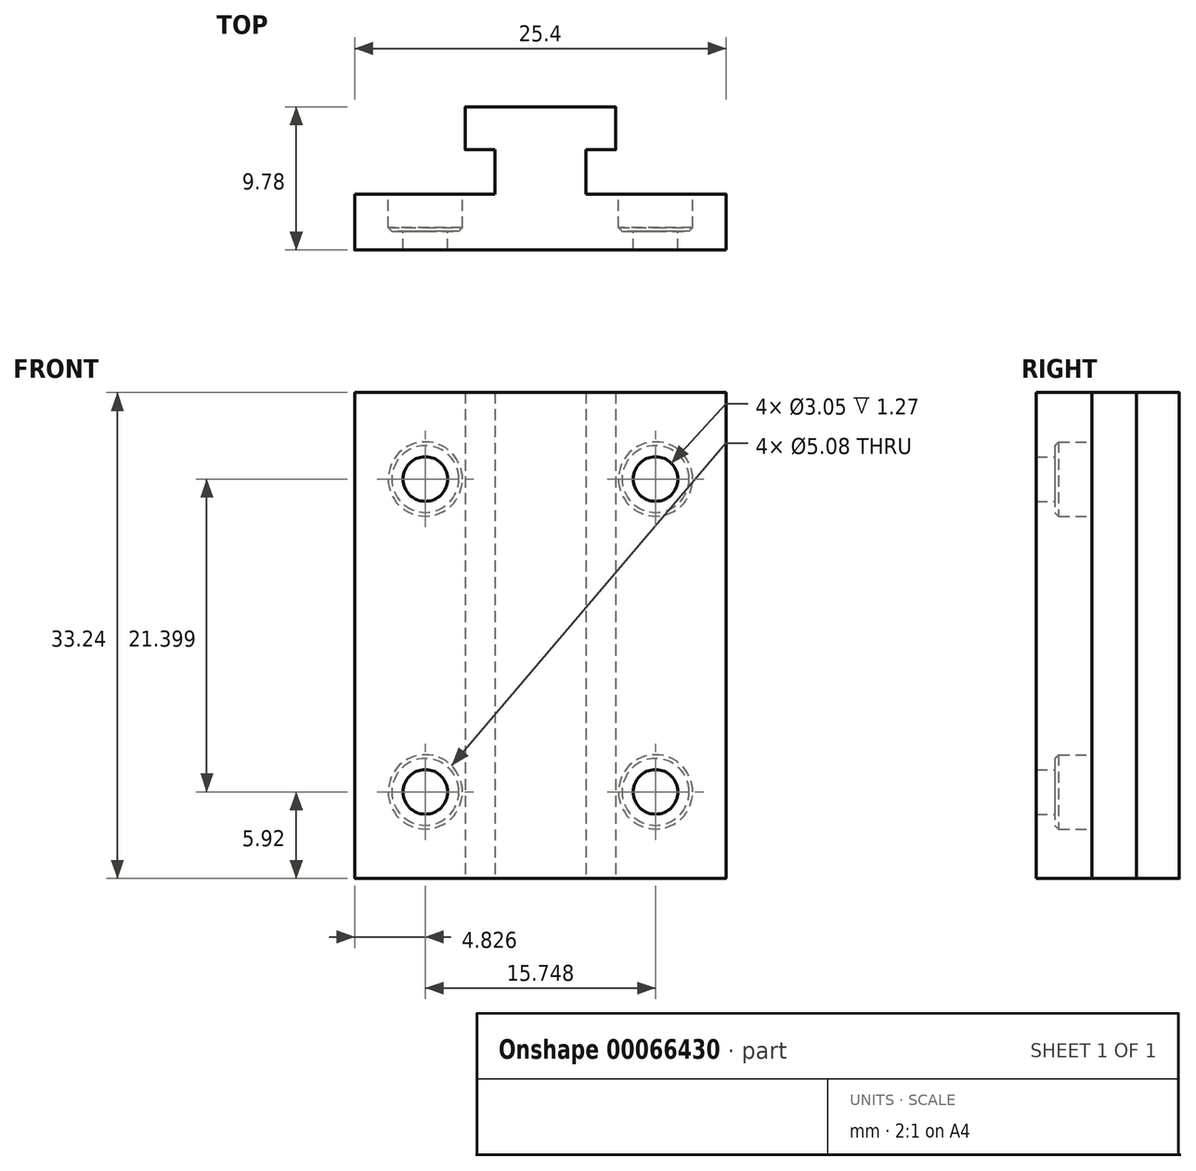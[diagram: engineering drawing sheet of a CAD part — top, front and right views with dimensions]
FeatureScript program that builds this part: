
annotation { "Feature Type Name" : "Feature", "Feature Type Description" : "" }
export const myFeature = defineFeature(function(context is Context, id is Id, definition is map)
    precondition{}
    {
        {
            var Q0;
            Q0=qCreatedBy(makeId("Front.planeOp"),FACE);
            var sketch = newSketch(context, id + "F0", { "sketchPlane" : qUnion([Q0])});
            skLineSegment(sketch, "E0.rect.bottom", {"start": v(5.16, 16.62) * mm, "end": v(-5.16, 16.62) * mm});
            skLineSegment(sketch, "E0.rect.top", {"start": v(5.16, -16.62) * mm, "end": v(-5.16, -16.62) * mm});
            skLineSegment(sketch, "E0.rect.left", {"start": v(5.16, 16.62) * mm, "end": v(5.16, -16.62) * mm});
            skLineSegment(sketch, "E0.rect.right", {"start": v(-5.16, 16.62) * mm, "end": v(-5.16, -16.62) * mm});
            skPoint(sketch, "E0.rect.middle", {"position": v(0, 0) * mm});
            skSolve(sketch);
        }
        {
            var Q0;
            Q0=qSketchRegion(id+"F0",true);
            extrude(context, id + "F1", {"entities" : qUnion([Q0]), "depth" : 2.92 * mm, "offsetDistance" : 25.4 * mm});
        }
        {
            var Q0;
            Q0=makeQuery(id+"F1.opExtrude","CAP_FACE",FACE,{"disambiguationData":[OSD([sQuery(id+"F0.wireOp",EDGE,"E0.rect.bottom"),sQuery(id+"F0.wireOp",EDGE,"E0.rect.top"),sQuery(id+"F0.wireOp",EDGE,"E0.rect.left"),sQuery(id+"F0.wireOp",EDGE,"E0.rect.right")])],"isStart":false});
            var sketch = newSketch(context, id + "F2", { "sketchPlane" : qUnion([Q0])});
            skLineSegment(sketch, "E1.rect.bottom", {"start": v(3.1, 16.62) * mm, "end": v(-3.1, 16.62) * mm});
            skLineSegment(sketch, "E1.rect.top", {"start": v(3.1, -16.62) * mm, "end": v(-3.1, -16.62) * mm});
            skLineSegment(sketch, "E1.rect.left", {"start": v(3.1, 16.62) * mm, "end": v(3.1, -16.62) * mm});
            skLineSegment(sketch, "E1.rect.right", {"start": v(-3.1, 16.62) * mm, "end": v(-3.1, -16.62) * mm});
            skPoint(sketch, "E1.rect.middle", {"position": v(0, 0) * mm});
            skSolve(sketch);
        }
        {
            var Q0;
            Q0=qSketchRegion(id+"F2",true);
            extrude(context, id + "F3", {"entities" : qUnion([Q0]), "operationType" : NewBodyOperationType.ADD, "depth" : 3.05 * mm, "offsetDistance" : 25.4 * mm});
        }
        {
            var Q0;
            Q0=makeQuery(id+"F3.opExtrude","CAP_FACE",FACE,{"disambiguationData":[OSD([sQuery(id+"F2.wireOp",EDGE,"E1.rect.bottom"),sQuery(id+"F2.wireOp",EDGE,"E1.rect.top"),sQuery(id+"F2.wireOp",EDGE,"E1.rect.left"),sQuery(id+"F2.wireOp",EDGE,"E1.rect.right")])],"isStart":false});
            var sketch = newSketch(context, id + "F4", { "sketchPlane" : qUnion([Q0])});
            skLineSegment(sketch, "E2.bottom", {"start": v(-12.7, -16.62) * mm, "end": v(12.7, -16.62) * mm});
            skLineSegment(sketch, "E2.top", {"start": v(-12.7, 16.62) * mm, "end": v(12.7, 16.62) * mm});
            skLineSegment(sketch, "E2.left", {"start": v(-12.7, -16.62) * mm, "end": v(-12.7, 16.62) * mm});
            skLineSegment(sketch, "E2.right", {"start": v(12.7, -16.62) * mm, "end": v(12.7, 16.62) * mm});
            skCircle(sketch, "E3", {"center": v(7.87, 10.7) * mm, "radius": 1.52 * mm});
            skCircle(sketch, "E4", {"center": v(7.87, -10.7) * mm, "radius": 1.52 * mm});
            skCircle(sketch, "E5", {"center": v(-7.87, -10.7) * mm, "radius": 1.52 * mm});
            skCircle(sketch, "E6", {"center": v(-7.87, 10.7) * mm, "radius": 1.52 * mm});
            skLineSegment(sketch, "E7", {"start": v(-7.87, -10.7) * mm, "end": v(7.87, -10.7) * mm, "construction": true});
            skPoint(sketch, "E8", {"position": v(0, -10.7) * mm});
            skLineSegment(sketch, "E9", {"start": v(7.87, 10.7) * mm, "end": v(7.87, -10.7) * mm, "construction": true});
            skPoint(sketch, "E10", {"position": v(7.87, 0) * mm});
            skSolve(sketch);
        }
        {
            var Q0;
            Q0=qSketchRegion(id+"F4",true);
            extrude(context, id + "F5", {"entities" : qUnion([Q0]), "operationType" : NewBodyOperationType.ADD, "depth" : 3.8 * mm, "offsetDistance" : 25.4 * mm});
        }
        {
            var Q0;
            Q0=makeQuery(id+"F1.opExtrude","CAP_EDGE",EDGE,{"disambiguationData":[OSD([sQuery(id+"F0.wireOp",EDGE,"E0.rect.left")])],"isStart":false});
            var Q1;
            Q1=makeQuery(id+"F1.opExtrude","CAP_EDGE",EDGE,{"disambiguationData":[OSD([sQuery(id+"F0.wireOp",EDGE,"E0.rect.left")])],"isStart":true});
            var Q2;
            Q2=makeQuery(id+"F1.opExtrude","CAP_EDGE",EDGE,{"disambiguationData":[OSD([sQuery(id+"F0.wireOp",EDGE,"E0.rect.right")])],"isStart":false});
            var Q3;
            Q3=makeQuery(id+"F1.opExtrude","CAP_EDGE",EDGE,{"disambiguationData":[OSD([sQuery(id+"F0.wireOp",EDGE,"E0.rect.right")])],"isStart":true});
            var Q4;
            Q4=makeQuery(id+"F1.opExtrude","CAP_EDGE",EDGE,{"disambiguationData":[OSD([sQuery(id+"F0.wireOp",EDGE,"E0.rect.top")])],"isStart":true});
            var Q5;
            Q5=makeQuery(id+"F1.opExtrude","CAP_EDGE",EDGE,{"disambiguationData":[OSD([sQuery(id+"F0.wireOp",EDGE,"E0.rect.bottom")])],"isStart":true});
            var Q6;
            Q6=makeQuery(id+"F5.opExtrude","SWEPT_EDGE",EDGE,{"disambiguationData":[OSD([sQuery(id+"F4.wireOp",EDGE,"E2.bottom"),sQuery(id+"F4.wireOp",EDGE,"E2.right")])]});
            var Q7;
            Q7=makeQuery(id+"F5.opExtrude","SWEPT_EDGE",EDGE,{"disambiguationData":[OSD([sQuery(id+"F4.wireOp",EDGE,"E2.bottom"),sQuery(id+"F4.wireOp",EDGE,"E2.left")])]});
            var Q8;
            Q8=makeQuery(id+"F5.opExtrude","SWEPT_EDGE",EDGE,{"disambiguationData":[OSD([sQuery(id+"F4.wireOp",EDGE,"E2.top"),sQuery(id+"F4.wireOp",EDGE,"E2.left")])]});
            var Q9;
            Q9=makeQuery(id+"F5.opExtrude","SWEPT_EDGE",EDGE,{"disambiguationData":[OSD([sQuery(id+"F4.wireOp",EDGE,"E2.top"),sQuery(id+"F4.wireOp",EDGE,"E2.right")])]});
            fillet(context, id + "F6", {"entities" : qUnion([Q0, Q1, Q2, Q3, Q4, Q5, Q6, Q7, Q8, Q9]), "radius" : .63 / 50.8 * mm, "tangentPropagation" : true, "allowEdgeOverflow" : false});
        }
        {
            var Q0;
            {var subQ0=sQuery(id+"F4.wireOp",EDGE,"E3");var subQ1=sQuery(id+"F4.wireOp",EDGE,"E2.right");var subQ2=sQuery(id+"F4.wireOp",EDGE,"E2.bottom");var subQ3=sQuery(id+"F4.wireOp",EDGE,"E2.top");var subQ4=sQuery(id+"F4.wireOp",EDGE,"E4");Q0=makeQuery(id+"F5.boolean.opBoolean","SPLIT",FACE,{"disambiguationData":[TD([makeQuery(id+"F3.opExtrude","SWEPT_FACE",FACE,{"disambiguationData":[OSD([sQuery(id+"F2.wireOp",EDGE,"E1.rect.left")])]})])],"derivedFrom":makeQuery(id+"F5.opExtrude","CAP_FACE",FACE,{"disambiguationData":[OSD([subQ2,subQ3,sQuery(id+"F4.wireOp",EDGE,"E2.left"),subQ1,subQ0,subQ4,sQuery(id+"F4.wireOp",EDGE,"E5"),sQuery(id+"F4.wireOp",EDGE,"E6")])],"isStart":true})});}
            var sketch = newSketch(context, id + "F7", { "sketchPlane" : qUnion([Q0])});
            skCircle(sketch, "E11", {"center": v(-7.87, 10.7) * mm, "radius": 2.54 * mm});
            skCircle(sketch, "E12", {"center": v(7.87, -10.7) * mm, "radius": 2.54 * mm});
            skCircle(sketch, "E13", {"center": v(-7.87, -10.7) * mm, "radius": 2.54 * mm});
            skCircle(sketch, "E14", {"center": v(7.87, 10.7) * mm, "radius": 2.54 * mm});
            skSolve(sketch);
        }
        {
            var Q0;
            Q0 = qSketchRegion(id + "F7", true);
            extrude(context, id + "F8", {"entities" : qUnion([Q0]), "operationType" : NewBodyOperationType.REMOVE, "oppositeDirection" : true, "depth" : 2.54 * mm, "offsetDistance" : 25.4 * mm});
        }
        {
            var Q0;
            Q0=makeQuery(id+"F8.boolean.opBoolean","COPY",EDGE,{"derivedFrom":makeQuery(id+"F8.opExtrude","CAP_EDGE",EDGE,{"disambiguationData":[OSD([sQuery(id+"F7.wireOp",EDGE,"E14")])],"isStart":false})});
            var Q1;
            Q1=makeQuery(id+"F8.boolean.opBoolean","COPY",EDGE,{"derivedFrom":makeQuery(id+"F8.opExtrude","CAP_EDGE",EDGE,{"disambiguationData":[OSD([sQuery(id+"F7.wireOp",EDGE,"E11")])],"isStart":false})});
            var Q2;
            Q2=makeQuery(id+"F8.boolean.opBoolean","COPY",EDGE,{"derivedFrom":makeQuery(id+"F8.opExtrude","CAP_EDGE",EDGE,{"disambiguationData":[OSD([sQuery(id+"F7.wireOp",EDGE,"E12")])],"isStart":false})});
            var Q3;
            Q3=makeQuery(id+"F8.boolean.opBoolean","COPY",EDGE,{"derivedFrom":makeQuery(id+"F8.opExtrude","CAP_EDGE",EDGE,{"disambiguationData":[OSD([sQuery(id+"F7.wireOp",EDGE,"E13")])],"isStart":false})});
            chamfer(context, id + "F9", {"entities" : qUnion([Q0, Q1, Q2, Q3]), "width" : 0.25 * mm, "tangentPropagation" : true});
        }
    });
